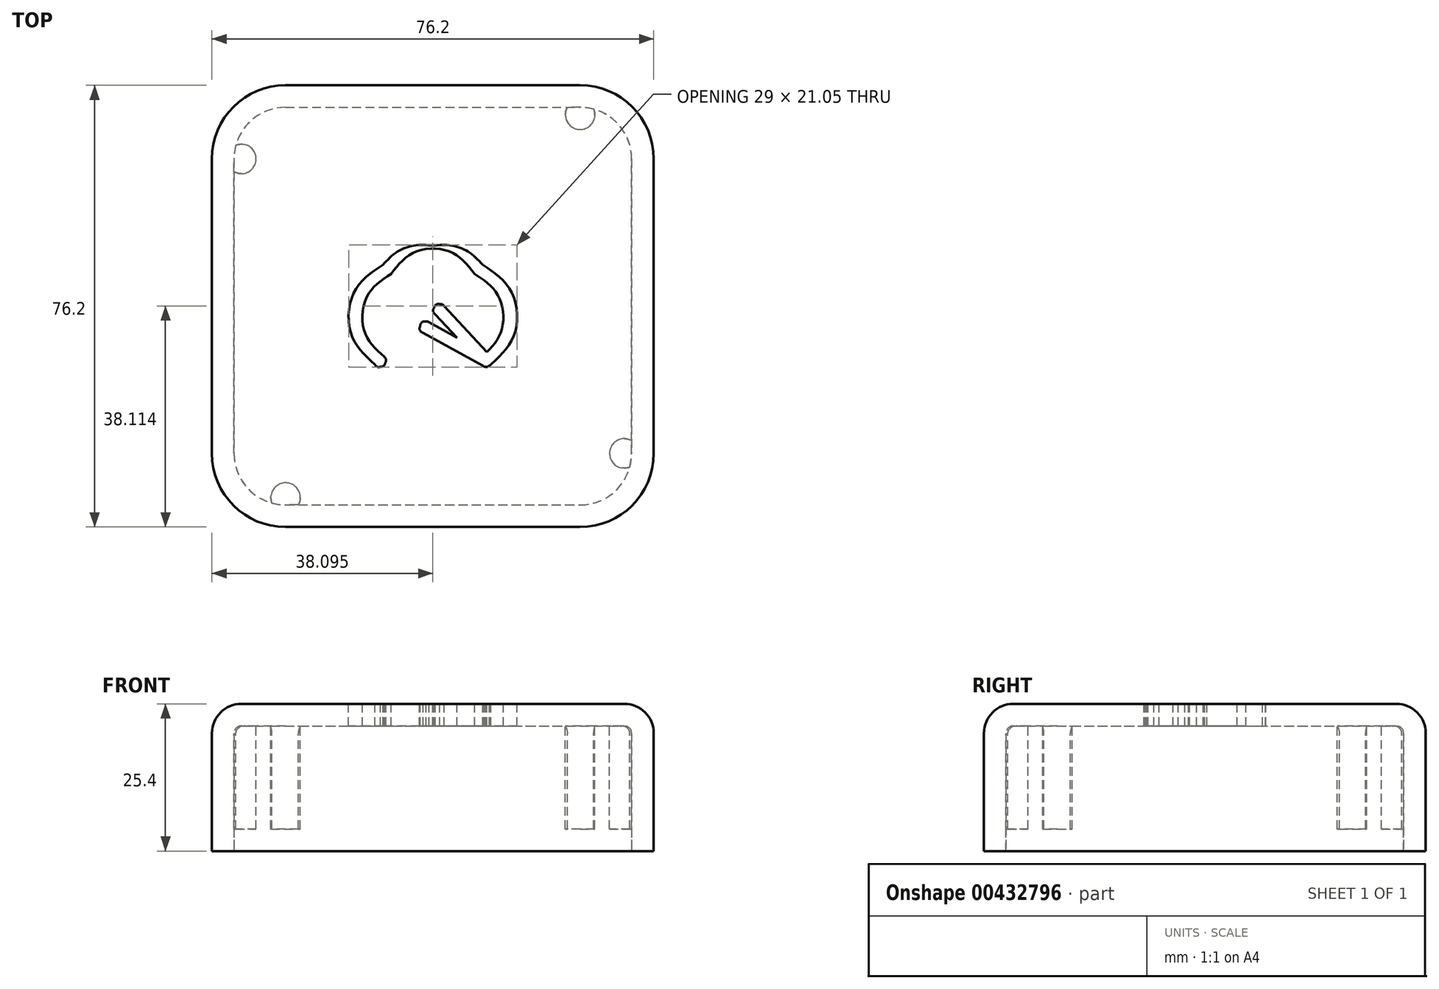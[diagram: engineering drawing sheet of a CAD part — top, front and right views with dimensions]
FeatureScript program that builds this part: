
annotation { "Feature Type Name" : "Feature", "Feature Type Description" : "" }
export const myFeature = defineFeature(function(context is Context, id is Id, definition is map)
    precondition{}
    {
        {
            var Q0;
            Q0=qCreatedBy(makeId("Top.planeOp"),FACE);
            var sketch = newSketch(context, id + "F0", { "sketchPlane" : qUnion([Q0])});
            skLineSegment(sketch, "E0.bottom", {"start": v(-25.4, 38.1) * mm, "end": v(25.4, 38.1) * mm});
            skLineSegment(sketch, "E0.top", {"start": v(-25.4, -38.1) * mm, "end": v(25.4, -38.1) * mm});
            skLineSegment(sketch, "E0.left", {"start": v(-38.1, 25.4) * mm, "end": v(-38.1, -25.4) * mm});
            skLineSegment(sketch, "E0.right", {"start": v(38.1, 25.4) * mm, "end": v(38.1, -25.4) * mm});
            skPoint(sketch, "E1.visualSharp", {"position": v(-38.1, 38.1) * mm});
            skArc(sketch, "E1.filletArc", {"start": v(-25.4, 38.1) * mm, "mid": v(-34.38, 34.38) * mm, "end": v(-38.1, 25.4) * mm});
            skPoint(sketch, "E2.visualSharp", {"position": v(-38.1, -38.1) * mm});
            skArc(sketch, "E2.filletArc", {"start": v(-38.1, -25.4) * mm, "mid": v(-34.38, -34.38) * mm, "end": v(-25.4, -38.1) * mm});
            skPoint(sketch, "E3.visualSharp", {"position": v(38.1, -38.1) * mm});
            skArc(sketch, "E3.filletArc", {"start": v(25.4, -38.1) * mm, "mid": v(34.38, -34.38) * mm, "end": v(38.1, -25.4) * mm});
            skPoint(sketch, "E4.visualSharp", {"position": v(38.1, 38.1) * mm});
            skArc(sketch, "E4.filletArc", {"start": v(38.1, 25.4) * mm, "mid": v(34.38, 34.38) * mm, "end": v(25.4, 38.1) * mm});
            skLineSegment(sketch, "E5", {"start": v(-38.1, 25.4) * mm, "end": v(38.1, -25.4) * mm, "construction": true});
            skLineSegment(sketch, "E6", {"start": v(38.1, 25.4) * mm, "end": v(-38.1, -25.4) * mm, "construction": true});
            skLineSegment(sketch, "E7", {"start": v(0, 0) * mm, "end": v(0, 24.1) * mm, "construction": true});
            skSolve(sketch);
        }
        {
            var Q0;
            Q0=makeQuery(id+"F0.imprint","IMPRINT",FACE,{"disambiguationData":[TD([[makeQuery(id+"F0.imprint","IMPRINT",EDGE,{"derivedFrom":sQuery(id+"F0.wireOp",EDGE,"E0.bottom")}),-1.0]])]});
            extrude(context, id + "F1", {"entities" : qUnion([Q0]), "depth" : 25.4 * mm});
        }
        {
            var Q0;
            Q0=makeQuery(id+"F1.opExtrude","CAP_FACE",FACE,{"disambiguationData":[OSD([sQuery(id+"F0.wireOp",EDGE,"E0.bottom"),sQuery(id+"F0.wireOp",EDGE,"E0.top"),sQuery(id+"F0.wireOp",EDGE,"E0.left"),sQuery(id+"F0.wireOp",EDGE,"E0.right"),sQuery(id+"F0.wireOp",EDGE,"E1.filletArc"),sQuery(id+"F0.wireOp",EDGE,"E2.filletArc"),sQuery(id+"F0.wireOp",EDGE,"E3.filletArc"),sQuery(id+"F0.wireOp",EDGE,"E4.filletArc")])],"isStart":false});
            fillet(context, id + "F2", {"entities" : qUnion([Q0]), "radius" : 5.08 * mm, "tangentPropagation" : true, "allowEdgeOverflow" : false});
        }
        {
            var Q0;
            Q0=makeQuery(id+"F1.opExtrude","CAP_FACE",FACE,{"disambiguationData":[OSD([sQuery(id+"F0.wireOp",EDGE,"E0.bottom"),sQuery(id+"F0.wireOp",EDGE,"E0.top"),sQuery(id+"F0.wireOp",EDGE,"E0.left"),sQuery(id+"F0.wireOp",EDGE,"E0.right"),sQuery(id+"F0.wireOp",EDGE,"E1.filletArc"),sQuery(id+"F0.wireOp",EDGE,"E2.filletArc"),sQuery(id+"F0.wireOp",EDGE,"E3.filletArc"),sQuery(id+"F0.wireOp",EDGE,"E4.filletArc")])],"isStart":true});
            shell(context, id + "F3", {"entities" : qUnion([Q0]), "thickness" : 3.8 * mm});
        }
        {
            var Q0;
            Q0=makeQuery(id+"F1.opExtrude","CAP_FACE",FACE,{"disambiguationData":[OSD([sQuery(id+"F0.wireOp",EDGE,"E0.bottom"),sQuery(id+"F0.wireOp",EDGE,"E0.top"),sQuery(id+"F0.wireOp",EDGE,"E0.left"),sQuery(id+"F0.wireOp",EDGE,"E0.right"),sQuery(id+"F0.wireOp",EDGE,"E1.filletArc"),sQuery(id+"F0.wireOp",EDGE,"E2.filletArc"),sQuery(id+"F0.wireOp",EDGE,"E3.filletArc"),sQuery(id+"F0.wireOp",EDGE,"E4.filletArc")])],"isStart":false});
            var sketch = newSketch(context, id + "F4", { "sketchPlane" : qUnion([Q0])});
            skFitSpline(sketch, "E8", {"points": [v(0, 10.47) * mm, v(-3.1, 10.47) * mm, v(-6.18, 9.35) * mm, v(-8.61, 7.1) * mm]});
            skFitSpline(sketch, "E9", {"points": [v(-8.61, 7.1) * mm, v(-13.47, 2.63) * mm, v(-14.08, -4.85) * mm, v(-10.01, -10.05) * mm]});
            skFitSpline(sketch, "E10", {"points": [v(-10.01, -10.05) * mm, v(-9.78, -10.35) * mm, v(-9.41, -10.5) * mm, v(-9.04, -10.46) * mm]});
            skFitSpline(sketch, "E11", {"points": [v(-9.04, -10.46) * mm, v(-8.67, -10.4) * mm, v(-8.35, -10.16) * mm, v(-8.21, -9.8) * mm]});
            skFitSpline(sketch, "E12", {"points": [v(-8.21, -9.8) * mm, v(-8.07, -9.46) * mm, v(-8.13, -9.06) * mm, v(-8.37, -8.77) * mm]});
            skFitSpline(sketch, "E13", {"points": [v(-8.37, -8.77) * mm, v(-11.78, -4.4) * mm, v(-11.27, 1.82) * mm, v(-7.2, 5.57) * mm]});
            skFitSpline(sketch, "E14", {"points": [v(-7.2, 5.57) * mm, v(-3.12, 9.33) * mm, v(3.12, 9.33) * mm, v(7.2, 5.57) * mm]});
            skFitSpline(sketch, "E15", {"points": [v(7.2, 5.57) * mm, v(11.27, 1.82) * mm, v(11.78, -4.4) * mm, v(8.37, -8.77) * mm]});
            skFitSpline(sketch, "E16", {"points": [v(8.37, -8.77) * mm, v(8.13, -9.06) * mm, v(8.07, -9.46) * mm, v(8.21, -9.8) * mm]});
            skFitSpline(sketch, "E17", {"points": [v(8.21, -9.8) * mm, v(8.35, -10.16) * mm, v(8.67, -10.4) * mm, v(9.04, -10.46) * mm]});
            skFitSpline(sketch, "E18", {"points": [v(9.04, -10.46) * mm, v(9.41, -10.5) * mm, v(9.78, -10.35) * mm, v(10.01, -10.05) * mm]});
            skFitSpline(sketch, "E19", {"points": [v(10.01, -10.05) * mm, v(14.08, -4.85) * mm, v(13.47, 2.63) * mm, v(8.61, 7.1) * mm]});
            skFitSpline(sketch, "E20", {"points": [v(8.61, 7.1) * mm, v(6.18, 9.35) * mm, v(3.1, 10.47) * mm, v(0, 10.47) * mm]});
            skFitSpline(sketch, "E21", {"points": [v(-1.15, -2.65) * mm, v(-1.63, -2.64) * mm, v(-2.05, -2.97) * mm, v(-2.18, -3.43) * mm]});
            skFitSpline(sketch, "E22", {"points": [v(-2.18, -3.43) * mm, v(-2.3, -3.9) * mm, v(-2.08, -4.4) * mm, v(-1.66, -4.62) * mm]});
            skFitSpline(sketch, "E23", {"points": [v(8.63, -10.3) * mm, v(8.96, -10.49) * mm, v(9.36, -10.48) * mm, v(9.68, -10.29) * mm]});
            skFitSpline(sketch, "E24", {"points": [v(9.68, -10.29) * mm, v(10, -10.1) * mm, v(10.2, -9.74) * mm, v(10.2, -9.37) * mm]});
            skFitSpline(sketch, "E25", {"points": [v(10.2, -9.37) * mm, v(10.18, -9) * mm, v(9.97, -8.65) * mm, v(9.64, -8.47) * mm]});
            skLineSegment(sketch, "E26", {"start": v(-1.66, -4.62) * mm, "end": v(8.63, -10.3) * mm});
            skLineSegment(sketch, "E27", {"start": v(8.63, -10.3) * mm, "end": v(-1.66, -4.62) * mm});
            skFitSpline(sketch, "E28", {"points": [v(-0.65, -2.8) * mm, v(-0.8, -2.7) * mm, v(-0.97, -2.66) * mm, v(-1.15, -2.65) * mm]});
            skLineSegment(sketch, "E29", {"start": v(9.64, -8.47) * mm, "end": v(-0.65, -2.8) * mm});
            skLineSegment(sketch, "E30", {"start": v(-0.65, -2.8) * mm, "end": v(9.64, -8.47) * mm});
            skFitSpline(sketch, "E31", {"points": [v(1.21, 0.34) * mm, v(0.79, 0.36) * mm, v(0.4, 0.12) * mm, v(0.23, -0.27) * mm]});
            skFitSpline(sketch, "E32", {"points": [v(0.23, -0.27) * mm, v(0.05, -0.66) * mm, v(0.13, -1.11) * mm, v(0.42, -1.42) * mm]});
            skFitSpline(sketch, "E33", {"points": [v(8.45, -10.04) * mm, v(8.7, -10.32) * mm, v(9.1, -10.44) * mm, v(9.46, -10.36) * mm]});
            skFitSpline(sketch, "E34", {"points": [v(9.46, -10.36) * mm, v(9.83, -10.27) * mm, v(10.12, -10) * mm, v(10.23, -9.64) * mm]});
            skFitSpline(sketch, "E35", {"points": [v(10.23, -9.64) * mm, v(10.34, -9.28) * mm, v(10.24, -8.89) * mm, v(9.98, -8.61) * mm]});
            skLineSegment(sketch, "E36", {"start": v(0.42, -1.42) * mm, "end": v(8.45, -10.04) * mm});
            skLineSegment(sketch, "E37", {"start": v(8.45, -10.04) * mm, "end": v(0.42, -1.42) * mm});
            skFitSpline(sketch, "E38", {"points": [v(1.95, 0) * mm, v(1.76, 0.21) * mm, v(1.5, 0.34) * mm, v(1.21, 0.34) * mm]});
            skLineSegment(sketch, "E39", {"start": v(9.98, -8.61) * mm, "end": v(1.95, 0) * mm});
            skLineSegment(sketch, "E40", {"start": v(1.95, 0) * mm, "end": v(9.98, -8.61) * mm});
            skSolve(sketch);
        }
        {
            var Q0;
            Q0=makeQuery(id+"F4.imprint","IMPRINT",FACE,{"disambiguationData":[TD([[makeQuery(id+"F4.imprint","IMPRINT",EDGE,{"derivedFrom":sQuery(id+"F4.wireOp",EDGE,"E31")}),1.0]])]});
            var Q1;
            Q1=makeQuery(id+"F4.imprint","IMPRINT",FACE,{"disambiguationData":[TD([[makeQuery(id+"F4.imprint","IMPRINT",EDGE,{"derivedFrom":sQuery(id+"F4.wireOp",EDGE,"E21")}),1.0]])]});
            var Q2;
            Q2=makeQuery(id+"F4.imprint","IMPRINT",FACE,{"disambiguationData":[TD([[makeQuery(id+"F4.imprint","IMPRINT",EDGE,{"derivedFrom":sQuery(id+"F4.wireOp",EDGE,"E8")}),1.0]])]});
            var Q3;
            {var subQ0=sQuery(id+"F4.wireOp",EDGE,"E16");var subQ1=sQuery(id+"F4.wireOp",EDGE,"E15");var subQ2=makeQuery(id+"F4.imprint","INTERSECT",VERTEX,{"derivedFrom":[subQ1,subQ0]});Q3=makeQuery(id+"F4.imprint","IMPRINT",FACE,{"disambiguationData":[TD([[makeQuery(id+"F4.imprint","IMPRINT",EDGE,{"disambiguationData":[TD([[subQ2,1.0]])],"derivedFrom":subQ1}),-1.0]])]});}
            var Q4;
            {var subQ0=sQuery(id+"F4.wireOp",EDGE,"E25");Q4=makeQuery(id+"F4.imprint","IMPRINT",FACE,{"disambiguationData":[TD([[makeQuery(id+"F4.imprint","IMPRINT",EDGE,{"derivedFrom":subQ0}),-1.0]])]});}
            var Q5;
            {var subQ0=sQuery(id+"F4.wireOp",EDGE,"E25");Q5=makeQuery(id+"F4.imprint","IMPRINT",FACE,{"disambiguationData":[TD([[makeQuery(id+"F4.imprint","IMPRINT",EDGE,{"derivedFrom":subQ0}),1.0]])]});}
            var Q6;
            {var subQ1=sQuery(id+"F4.wireOp",EDGE,"E23");Q6=makeQuery(id+"F4.imprint","IMPRINT",FACE,{"disambiguationData":[TD([[makeQuery(id+"F4.imprint","IMPRINT",EDGE,{"derivedFrom":subQ1}),1.0]])]});}
            extrude(context, id + "F5", {"entities" : qUnion([Q0, Q1, Q2, Q3, Q4, Q5, Q6]), "operationType" : NewBodyOperationType.REMOVE, "oppositeDirection" : true, "depth" : 25.4 * mm});
        }
        {
            var Q0;
            Q0=makeQuery(id+"F3.opShell","OFFSET_FACE",FACE,{"disambiguationData":[OSD([sQuery(id+"F0.wireOp",EDGE,"E0.bottom"),sQuery(id+"F0.wireOp",EDGE,"E0.top"),sQuery(id+"F0.wireOp",EDGE,"E0.left"),sQuery(id+"F0.wireOp",EDGE,"E0.right"),sQuery(id+"F0.wireOp",EDGE,"E1.filletArc"),sQuery(id+"F0.wireOp",EDGE,"E2.filletArc"),sQuery(id+"F0.wireOp",EDGE,"E3.filletArc"),sQuery(id+"F0.wireOp",EDGE,"E4.filletArc")])]});
            var sketch = newSketch(context, id + "F6", { "sketchPlane" : qUnion([Q0])});
            skCircle(sketch, "E41", {"center": v(-33.02, -25.4) * mm, "radius": 2.54 * mm});
            skCircle(sketch, "E42", {"center": v(-25.4, 33.02) * mm, "radius": 2.54 * mm});
            skCircle(sketch, "E43", {"center": v(33.02, 25.4) * mm, "radius": 2.54 * mm});
            skCircle(sketch, "E44", {"center": v(25.4, -33.02) * mm, "radius": 2.54 * mm});
            skSolve(sketch);
        }
        {
            var Q0;
            Q0 = qSketchRegion(id + "F6", true);
            extrude(context, id + "F7", {"entities" : qUnion([Q0]), "operationType" : NewBodyOperationType.ADD, "depth" : 17.78 * mm});
        }
    });
